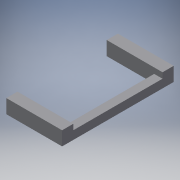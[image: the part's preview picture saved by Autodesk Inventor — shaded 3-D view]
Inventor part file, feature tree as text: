
AUTODESK INVENTOR PART (.ipt)
format: ipt  version: 2017 (Build 210142000, 142)  size: 145,408 bytes
history: native  units: mm
features: extrude x3, sketch x3, projected_geometry x3, other x3, reference x1
ambient origin geometry x8: Origin, YZ Plane, XZ Plane, XY Plane, X Axis, Y Axis, Z Axis, Center Point
bodies: Solid1 (feature_tree)
feature tree (13):
  extrude  "Extrusion1"  Depth=50.0mm TaperAngle=0.0deg
  extrude  "Extrusion2"  Depth=200.0mm TaperAngle=0.0deg
  extrude  "Extrusion3"  Depth=30.0mm
  sketch  "Sketch1"  dims[d0=200.0mm d1=50.0mm d2=0.0mm]
  reference  "Reference1"
  sketch  "Sketch2"  dims[d7=20.0mm d8=200.0mm d9=0.0mm]
  projected_geometry  "Projected Loop1"
  projected_geometry  "Projected Loop2"
  sketch  "Sketch3"  dims[d10=30.0mm d11=30.0mm d13=170.0mm d14=20.0mm d15=120.0mm d16=30.0mm d17=0.0mm]
  projected_geometry  "Projected Loop3"
  other  "<userpath>\OneDrive\Inventor\VolledigGeassembleerdv001.iam"
  other  "VolledigGeassembleerdv001.iam"
  other  "Frame:1"
